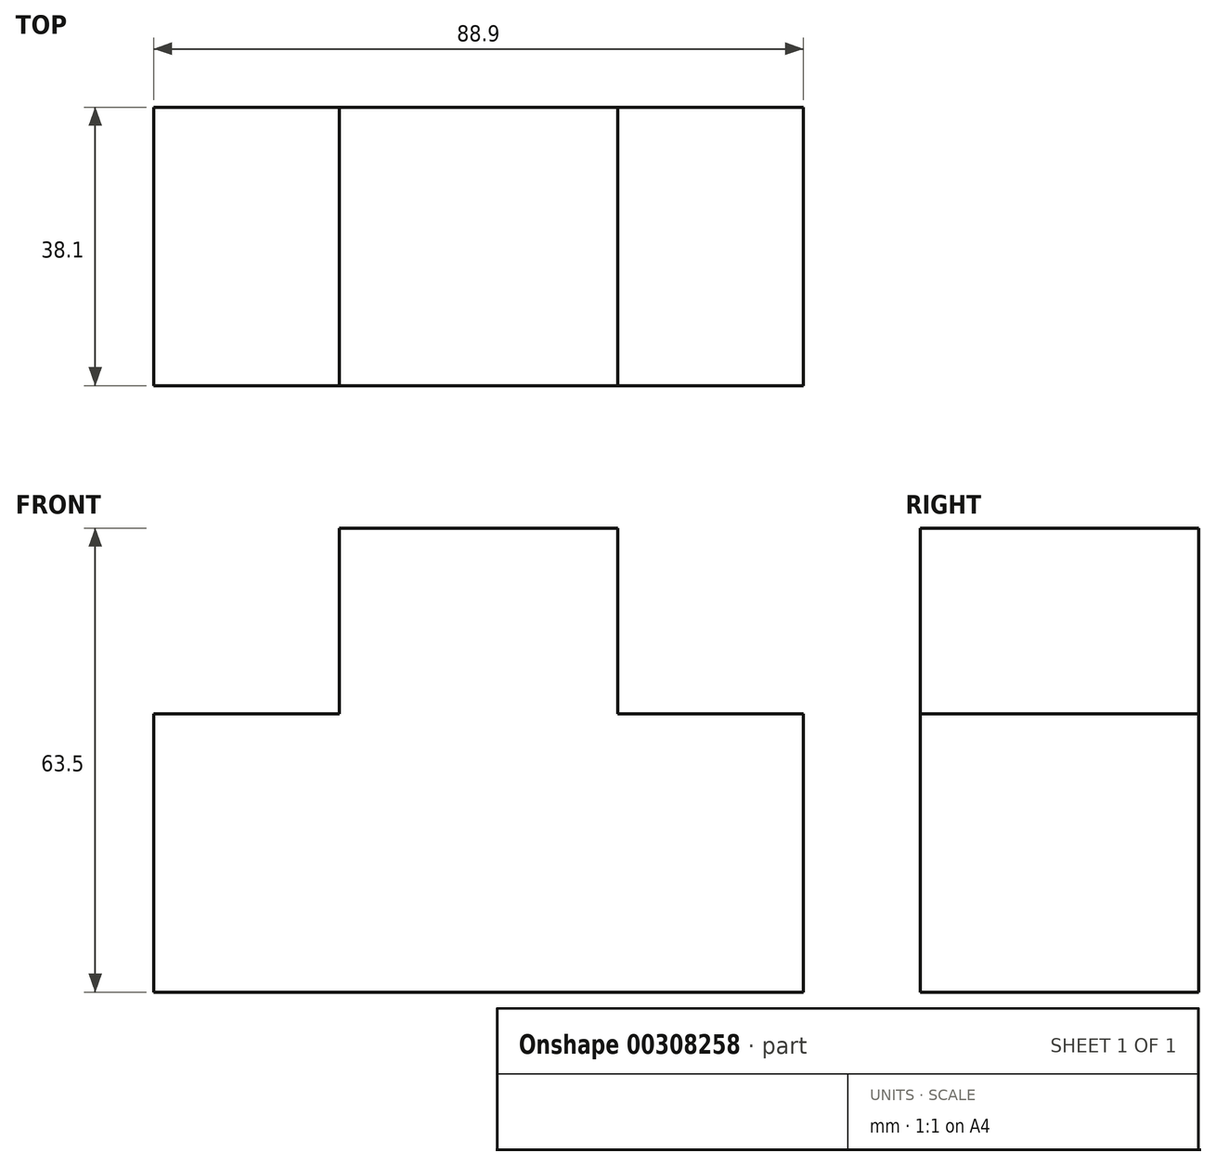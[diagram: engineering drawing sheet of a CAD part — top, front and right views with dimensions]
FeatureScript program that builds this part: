
annotation { "Feature Type Name" : "Feature", "Feature Type Description" : "" }
export const myFeature = defineFeature(function(context is Context, id is Id, definition is map)
    precondition{}
    {
        {
            var Q0;
            Q0=qCreatedBy(makeId("Front.planeOp"),FACE);
            var sketch = newSketch(context, id + "F0", { "sketchPlane" : qUnion([Q0])});
            skLineSegment(sketch, "E0", {"start": v(-45.34, -42.57) * mm, "end": v(43.56, -42.57) * mm});
            skLineSegment(sketch, "E1", {"start": v(43.56, -4.47) * mm, "end": v(18.16, -4.47) * mm});
            skLineSegment(sketch, "E2", {"start": v(18.16, -4.47) * mm, "end": v(18.16, 20.93) * mm});
            skLineSegment(sketch, "E3", {"start": v(18.16, 20.93) * mm, "end": v(-19.94, 20.93) * mm});
            skLineSegment(sketch, "E4", {"start": v(-19.94, 20.93) * mm, "end": v(-19.94, -4.47) * mm});
            skLineSegment(sketch, "E5", {"start": v(-19.94, -4.47) * mm, "end": v(-45.34, -4.47) * mm});
            skLineSegment(sketch, "E6", {"start": v(-45.34, -4.47) * mm, "end": v(-45.34, -42.57) * mm});
            skLineSegment(sketch, "E7", {"start": v(43.56, -4.47) * mm, "end": v(43.56, -42.57) * mm});
            skSolve(sketch);
        }
        {
            var Q0;
            Q0 = qSketchRegion(id + "F0", true);
            extrude(context, id + "F1", {"entities" : qUnion([Q0]), "depth" : 38.1 * mm});
        }
    });
